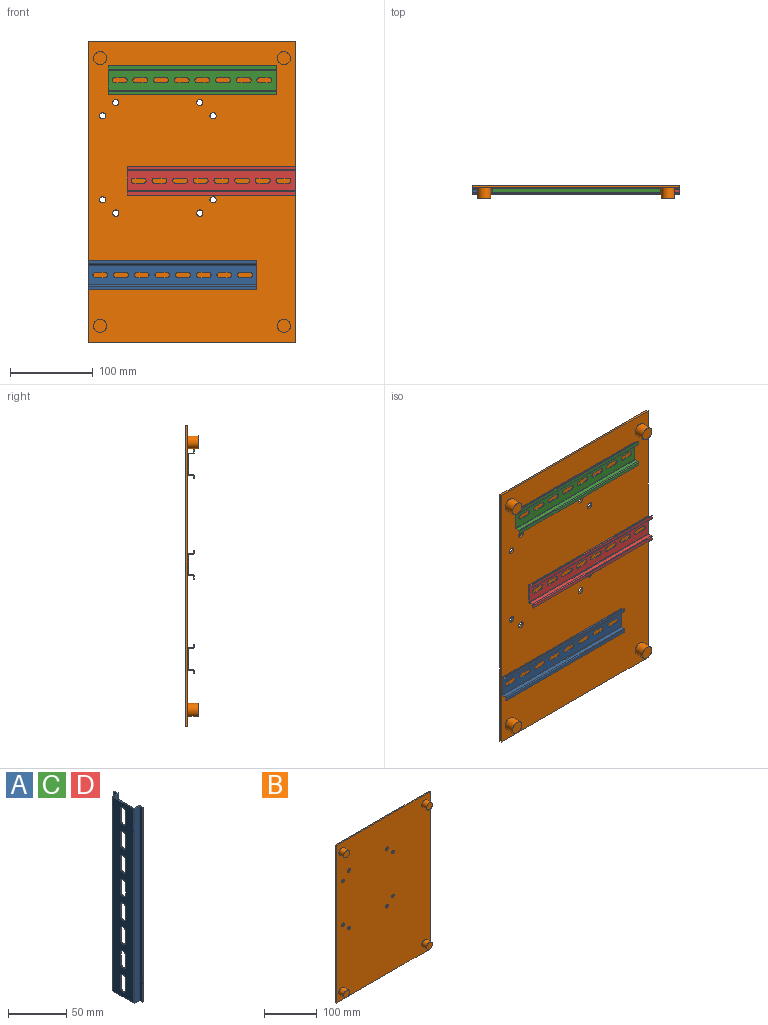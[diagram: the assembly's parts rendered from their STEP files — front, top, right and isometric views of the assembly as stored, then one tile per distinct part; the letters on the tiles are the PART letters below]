
ASSEMBLY  parts=4 mates=3
PART A: 54 faces, bbox 7.5x35x203.2 mm
  f0: plane 203.2x24mm, normal (1,0,0), area 4037.7mm2, adj f6,f7,f20,f21,f22,f23,f24,f25
  f1: plane 203.2x25mm, normal (-1,0,0), area 4240.9mm2, adj f15,f16,f20,f21,f22,f23,f24,f25
  f2: plane 203.2x1mm, normal (0,-1,0), area 203.2mm2, adj f3,f19,f52,f53
  f3: plane 203.2x4mm, normal (1,0,0), area 812.8mm2, adj f2,f4,f52,f53
  f4: cylinder r=1mm len=203.2mm, axis (0,0,-1), area 319.2mm2, adj f3,f5,f52,f53
  f5: plane 203.2x5mm, normal (0,1,0), area 1016mm2, adj f4,f6,f52,f53
  f6: cylinder r=0.5mm len=203.2mm, axis (0,0,-1), area 159.6mm2, adj f0,f5,f52,f53
  f7: cylinder r=0.5mm len=203.2mm, axis (0,0,-1), area 159.6mm2, adj f0,f8,f52,f53
  f8: plane 203.2x5mm, normal (0,-1,0), area 1016mm2, adj f7,f9,f52,f53
  f9: cylinder r=1mm len=203.2mm, axis (0,0,-1), area 319.2mm2, adj f8,f10,f52,f53
  f10: plane 203.2x4mm, normal (1,0,0), area 812.8mm2, adj f9,f11,f52,f53
  f11: plane 203.2x1mm, normal (0,1,0), area 203.2mm2, adj f10,f12,f52,f53
  f12: plane 203.2x3.5mm, normal (-1,0,0), area 711.2mm2, adj f11,f13,f52,f53
  f13: cylinder r=0.5mm len=203.2mm, axis (0,0,-1), area 159.6mm2, adj f12,f14,f52,f53
  f14: plane 203.2x5mm, normal (0,1,0), area 1016mm2, adj f13,f15,f52,f53
  f15: cylinder r=1mm len=203.2mm, axis (0,0,-1), area 319.2mm2, adj f1,f14,f52,f53
  f16: cylinder r=1mm len=203.2mm, axis (0,0,-1), area 319.2mm2, adj f1,f17,f52,f53
  f17: plane 203.2x5mm, normal (0,-1,0), area 1016mm2, adj f16,f18,f52,f53
  f18: cylinder r=0.5mm len=203.2mm, axis (0,0,-1), area 159.6mm2, adj f17,f19,f52,f53
  f19: plane 203.2x3.5mm, normal (-1,0,0), area 711.2mm2, adj f2,f18,f52,f53
  f20: cylinder r=3.15mm len=6.3mm, axis (-1,0,0), area 9.9mm2, adj f0,f1,f49,f51
  f21: cylinder r=3.15mm len=6.3mm, axis (-1,0,0), area 9.9mm2, adj f0,f1,f46,f48
  f22: cylinder r=3.15mm len=6.3mm, axis (-1,0,0), area 9.9mm2, adj f0,f1,f43,f45
  f23: cylinder r=3.15mm len=6.3mm, axis (-1,0,0), area 9.9mm2, adj f0,f1,f40,f42
  f24: cylinder r=3.15mm len=6.3mm, axis (-1,0,0), area 9.9mm2, adj f0,f1,f37,f39
  f25: cylinder r=3.15mm len=6.3mm, axis (-1,0,0), area 9.9mm2, adj f0,f1,f34,f36
  f26: cylinder r=3.15mm len=6.3mm, axis (-1,0,0), area 9.9mm2, adj f0,f1,f31,f33
  f27: cylinder r=3.15mm len=6.3mm, axis (-1,0,0), area 9.9mm2, adj f0,f1,f28,f30
  f28: plane 11.7x1mm, normal (0,-1,0), area 11.7mm2, adj f0,f1,f27,f29
  f29: cylinder r=3.15mm len=6.3mm, axis (-1,0,0), area 9.9mm2, adj f0,f1,f28,f30
  f30: plane 11.7x1mm, normal (0,1,0), area 11.7mm2, adj f0,f1,f27,f29
  f31: plane 11.7x1mm, normal (0,-1,0), area 11.7mm2, adj f0,f1,f26,f32
  f32: cylinder r=3.15mm len=6.3mm, axis (-1,0,0), area 9.9mm2, adj f0,f1,f31,f33
  f33: plane 11.7x1mm, normal (0,1,0), area 11.7mm2, adj f0,f1,f26,f32
  f34: plane 11.7x1mm, normal (0,-1,0), area 11.7mm2, adj f0,f1,f25,f35
  f35: cylinder r=3.15mm len=6.3mm, axis (-1,0,0), area 9.9mm2, adj f0,f1,f34,f36
  f36: plane 11.7x1mm, normal (0,1,0), area 11.7mm2, adj f0,f1,f25,f35
  f37: plane 11.7x1mm, normal (0,-1,0), area 11.7mm2, adj f0,f1,f24,f38
  f38: cylinder r=3.15mm len=6.3mm, axis (-1,0,0), area 9.9mm2, adj f0,f1,f37,f39
  f39: plane 11.7x1mm, normal (0,1,0), area 11.7mm2, adj f0,f1,f24,f38
  f40: plane 11.7x1mm, normal (0,-1,0), area 11.7mm2, adj f0,f1,f23,f41
  f41: cylinder r=3.15mm len=6.3mm, axis (-1,0,0), area 9.9mm2, adj f0,f1,f40,f42
  f42: plane 11.7x1mm, normal (0,1,0), area 11.7mm2, adj f0,f1,f23,f41
  f43: plane 11.7x1mm, normal (0,-1,0), area 11.7mm2, adj f0,f1,f22,f44
  f44: cylinder r=3.15mm len=6.3mm, axis (-1,0,0), area 9.9mm2, adj f0,f1,f43,f45
  f45: plane 11.7x1mm, normal (0,1,0), area 11.7mm2, adj f0,f1,f22,f44
  f46: plane 11.7x1mm, normal (0,-1,0), area 11.7mm2, adj f0,f1,f21,f47
  f47: cylinder r=3.15mm len=6.3mm, axis (-1,0,0), area 9.9mm2, adj f0,f1,f46,f48
  f48: plane 11.7x1mm, normal (0,1,0), area 11.7mm2, adj f0,f1,f21,f47
  f49: plane 11.7x1mm, normal (0,-1,0), area 11.7mm2, adj f0,f1,f20,f50
  f50: cylinder r=3.15mm len=6.3mm, axis (-1,0,0), area 9.9mm2, adj f0,f1,f49,f51
  f51: plane 11.7x1mm, normal (0,1,0), area 11.7mm2, adj f0,f1,f20,f50
  f52: plane 35x7.5mm, normal (0,0,1), area 47.4mm2, adj f0,f1,f2,f3,f4,f5,f6,f7
  f53: plane 35x7.5mm, normal (0,0,-1), area 47.4mm2, adj f0,f1,f2,f3,f4,f5,f6,f7
PART B: 22 faces, bbox 250.8x15.2x365.1 mm
  f0: plane 365.13x2.54mm, normal (1,0,0), area 927.4mm2, adj f1,f3,f4,f5
  f1: plane 250.83x2.54mm, normal (0,0,1), area 637.1mm2, adj f0,f2,f4,f5
  f2: plane 365.13x2.54mm, normal (-1,0,0), area 927.4mm2, adj f1,f3,f4,f5
  f3: plane 250.83x2.54mm, normal (0,0,-1), area 637.1mm2, adj f0,f2,f4,f5
  f4: plane 365.13x250.83mm, normal (0,1,0), area 91224.9mm2, adj f0,f1,f2,f3,f14,f15,f16,f17
  f5: plane 365.13x250.83mm, normal (0,-1,0), area 90433.2mm2, adj f0,f1,f2,f3,f7,f9,f11,f13
  f6: plane 15.88x15.88mm, normal (0,-1,0), area 197.9mm2, adj f7
  f7: cylinder r=7.94mm len=15.88mm, axis (0,1,0), area 633.4mm2, adj f5,f6
  f8: plane 15.88x15.88mm, normal (0,-1,0), area 197.9mm2, adj f9
  f9: cylinder r=7.94mm len=15.88mm, axis (0,1,0), area 633.4mm2, adj f5,f8
  f10: plane 15.88x15.88mm, normal (0,-1,0), area 197.9mm2, adj f11
  f11: cylinder r=7.94mm len=15.88mm, axis (0,1,0), area 633.4mm2, adj f5,f10
  f12: plane 15.88x15.88mm, normal (0,-1,0), area 197.9mm2, adj f13
  f13: cylinder r=7.94mm len=15.88mm, axis (0,1,0), area 633.4mm2, adj f5,f12
  f14: cylinder r=3.77mm len=7.54mm, axis (0,-1,0), area 60.2mm2, adj f4,f5
  f15: cylinder r=3.77mm len=7.54mm, axis (0,-1,0), area 60.2mm2, adj f4,f5
  f16: cylinder r=3.77mm len=7.54mm, axis (0,-1,0), area 60.2mm2, adj f4,f5
  f17: cylinder r=3.77mm len=7.54mm, axis (0,-1,0), area 60.2mm2, adj f4,f5
  f18: cylinder r=3.77mm len=7.54mm, axis (0,-1,0), area 60.2mm2, adj f4,f5
  f19: cylinder r=3.77mm len=7.54mm, axis (0,-1,0), area 60.2mm2, adj f4,f5
  f20: cylinder r=3.77mm len=7.54mm, axis (0,-1,0), area 60.2mm2, adj f4,f5
  f21: cylinder r=3.77mm len=7.54mm, axis (0,-1,0), area 60.2mm2, adj f4,f5
PART C: same geometry as A
PART D: same geometry as A
PLACE A rot(axis=(-0.58,0.58,-0.58),120deg) t=(-23.37,5,-117.09)mm
PLACE B t=(0,5,-16.76)mm
PLACE C rot(axis=(-0.58,0.58,-0.58),120deg) t=(0.01,5,118.4)mm
PLACE D rot(axis=(-0.58,0.58,-0.58),120deg) t=(23.05,5,-3.02)mm
MATE planar C.f1 <-> B.f5  axis (0,1,0) through (0.01,5,118.4)mm
MATE planar A.f1 <-> B.f5  axis (0,1,0) through (-23.37,5,-117.09)mm
MATE planar D.f1 <-> B.f5  axis (0,1,0) through (41.4,5,-6.17)mm
